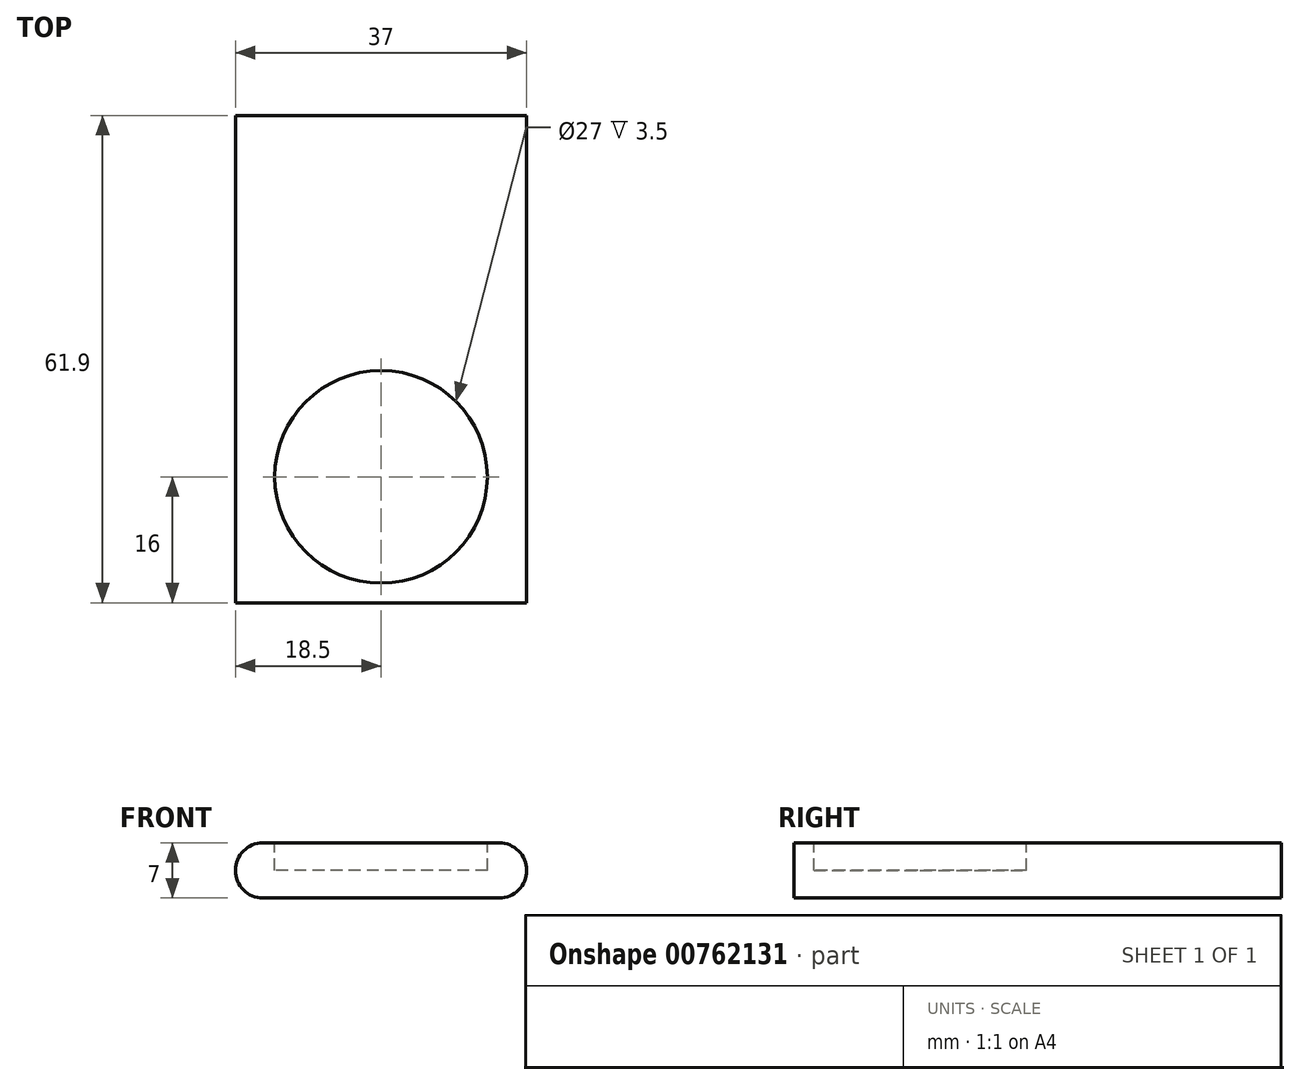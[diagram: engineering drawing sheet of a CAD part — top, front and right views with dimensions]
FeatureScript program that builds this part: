
annotation { "Feature Type Name" : "Feature", "Feature Type Description" : "" }
export const myFeature = defineFeature(function(context is Context, id is Id, definition is map)
    precondition{}
    {
        {
            var Q0;
            Q0=qCreatedBy(makeId("Front.planeOp"),FACE);
            var sketch = newSketch(context, id + "F0", { "sketchPlane" : qUnion([Q0])});
            skLineSegment(sketch, "E0.bottom", {"start": v(0, 0) * mm, "end": v(30, 0) * mm});
            skLineSegment(sketch, "E0.top", {"start": v(0, 7) * mm, "end": v(30, 7) * mm});
            skArc(sketch, "E1", {"start": v(0, 7) * mm, "mid": v(-3.5, 3.5) * mm, "end": v(0, 0) * mm});
            skArc(sketch, "E2", {"start": v(30, 7) * mm, "mid": v(33.5, 3.5) * mm, "end": v(30, 0) * mm});
            skSolve(sketch);
        }
        {
            var Q0;
            Q0=makeQuery(id+"F0.imprint","IMPRINT",FACE,{"disambiguationData":[TD([[makeQuery(id+"F0.imprint","IMPRINT",EDGE,{"derivedFrom":sQuery(id+"F0.wireOp",EDGE,"E0.bottom")}),1.0]])]});
            extrude(context, id + "F1", {"entities" : qUnion([Q0]), "depth" : 61.9 * mm, "offsetDistance" : 25 * mm});
        }
        {
            var Q0;
            Q0=makeQuery(id+"F1.opExtrude","SWEPT_FACE",FACE,{"disambiguationData":[OSD([sQuery(id+"F0.wireOp",EDGE,"E0.top")])]});
            var sketch = newSketch(context, id + "F2", { "sketchPlane" : qUnion([Q0])});
            skCircle(sketch, "E3", {"center": v(15, -45.9) * mm, "radius": 13.5 * mm});
            skLineSegment(sketch, "E4", {"start": v(15, -41.04) * mm, "end": v(15, -58.4) * mm, "construction": true});
            skSolve(sketch);
        }
        {
            var Q0;
            Q0=makeQuery(id+"F2.imprint","IMPRINT",FACE,{"disambiguationData":[TD([[makeQuery(id+"F2.imprint","IMPRINT",EDGE,{"derivedFrom":sQuery(id+"F2.wireOp",EDGE,"E3")}),1.0]])]});
            extrude(context, id + "F3", {"entities" : qUnion([Q0]), "operationType" : NewBodyOperationType.REMOVE, "oppositeDirection" : true, "depth" : 3.5 * mm, "offsetDistance" : 25 * mm});
        }
    });
